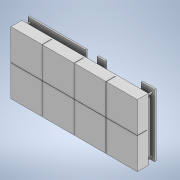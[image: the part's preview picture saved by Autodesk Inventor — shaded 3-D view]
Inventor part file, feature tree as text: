
AUTODESK INVENTOR PART (.ipt)
format: ipt  version: 2021 (Build 250183000, 183)  size: 385,024 bytes
history: native  units: mm
features: sketch x17, extrude x15, hole x1, fillet x1, chamfer x1
ambient origin geometry x8: Origin, YZ Plane, XZ Plane, XY Plane, X Axis, Y Axis, Z Axis, Center Point
bodies: Solid1 (feature_tree)
feature tree (35):
  extrude  "Extrusion1"  Depth=40.0mm
  extrude  "Extrusion2"  Depth=20.0mm
  extrude  "Extrusion3"  Depth=19.9mm
  extrude  "Extrusion4"  Depth=6.0mm TaperAngle=0.0deg
  extrude  "Extrusion5"  Depth=0.2mm
  extrude  "Extrusion6"  Depth=19.9mm
  hole  "Hole1"  [1 undecoded]
  extrude  "Extrusion8"  Depth=6.0mm TaperAngle=0.0deg
  sketch  "Sketch10"  dims[d19=0.5mm d20=2.0mm]
  extrude  "Extrusion9"  Depth=2.0mm
  extrude  "Extrusion10"  Depth=0.5mm
  extrude  "Extrusion11"  Depth=1.0mm
  extrude  "Extrusion12"  Depth=1.0mm TaperAngle=0.0deg
  extrude  "Extrusion13"  Depth=7.5mm
  extrude  "Extrusion14"  Depth=1.0mm TaperAngle=0.0deg
  fillet  "Fillet1"  Radius=5.0mm
  extrude  "Extrusion15"  Depth=5.0mm
  chamfer  "Chamfer1"  Distance=5.0mm
  extrude  "Extrusion16"  Depth=5.0mm
  sketch  "Sketch1"  dims[d0=81.0mm d1=40.0mm]
  sketch  "Sketch2"  dims[d2=20.0mm d3=40.5mm]
  sketch  "Sketch3"  dims[d4=7.0mm d5=0.0mm d6=19.9mm]
  sketch  "Sketch4"  dims[d7=19.9mm d8=6.0mm d9=0.0mm]
  sketch  "Sketch5"  dims[d10=0.2mm d11=0.2mm]
  sketch  "Sketch6"  dims[d12=0.2mm d13=19.9mm]
  sketch  "Sketch8"  dims[d14=19.9mm d15=40.4mm]
  sketch  "Sketch9"  dims[d16=40.4mm d17=6.0mm d18=0.0mm]
  sketch  "Sketch11"  dims[d21=2.0mm d22=0.5mm]
  sketch  "Sketch12"  dims[d23=1.0mm d24=1.0mm]
  sketch  "Sketch13"  dims[d25=5.0mm d26=0.0mm d27=1.0mm d28=0.0mm]
  sketch  "Sketch14"  dims[d29=7.5mm d30=3.75mm]
  sketch  "Sketch15"  dims[d31=18.0mm d32=1.0mm d33=0.0mm d39=5.0mm]
  sketch  "Sketch16"  dims[d40=35.0mm d41=5.0mm]
  sketch  "Sketch17"  dims[d42=5.0mm]
  sketch  "Sketch18"  dims[d43=40.5mm d44=5.0mm d45=5.0mm d46=76.03mm d47=76.03mm d48=35.0mm d49=23.0mm d50=23.0mm d51=35.0mm d52=35.0mm d53=34.0mm d54=34.0mm d55=47.0mm d56=47.0mm d57=2.0mm d58=6.0mm d59=4.0mm d60=2.0mm d61=90.0deg d62=1.0mm d63=20.594885mm d64=0.5mm d65=5.0mm d66=0.0mm d67=4.2mm d68=13.0mm d69=3.0mm d70=4.2mm d71=13.0mm d72=3.0mm d73=1.0mm d74=0.0mm d75=5.2mm d76=12.44mm d77=23.1mm d78=4.5mm d79=0.0mm d80=1.0mm d81=1.0mm d82=1.0mm d83=3.0mm d84=2.0mm d85=0.0mm d86=22.4mm d87=37.6mm d88=43.0mm d89=58.3mm d90=2.7mm d91=6.2mm d92=0.3mm d93=0.3mm d94=0.3mm d95=0.3mm d96=0.3mm d97=0.3mm d98=6.0mm d99=0.0mm d100=1.0mm d101=1.0mm d102=1.0mm d103=1.0mm d104=1.0mm d105=1.0mm d106=1.0mm d107=1.0mm d108=5.0mm d109=3.0mm d110=0.0mm d111=40.5mm d112=15.0mm d113=6.0mm d114=8.3mm d115=0.0mm d116=0.5mm d117=3.2mm d118=3.2mm d119=3.2mm d120=3.2mm d121=1.0mm d122=0.0mm d123=1.0mm d124=2.0mm d125=45.0deg d126=1.0mm d127=1.0mm d128=1.0mm d129=0.0mm]
note: 1 required parameter value undecoded (feature->parameter linkage not recoverable at this tier; creation-order binding heuristic only, values carry confidence <= 0.55)
